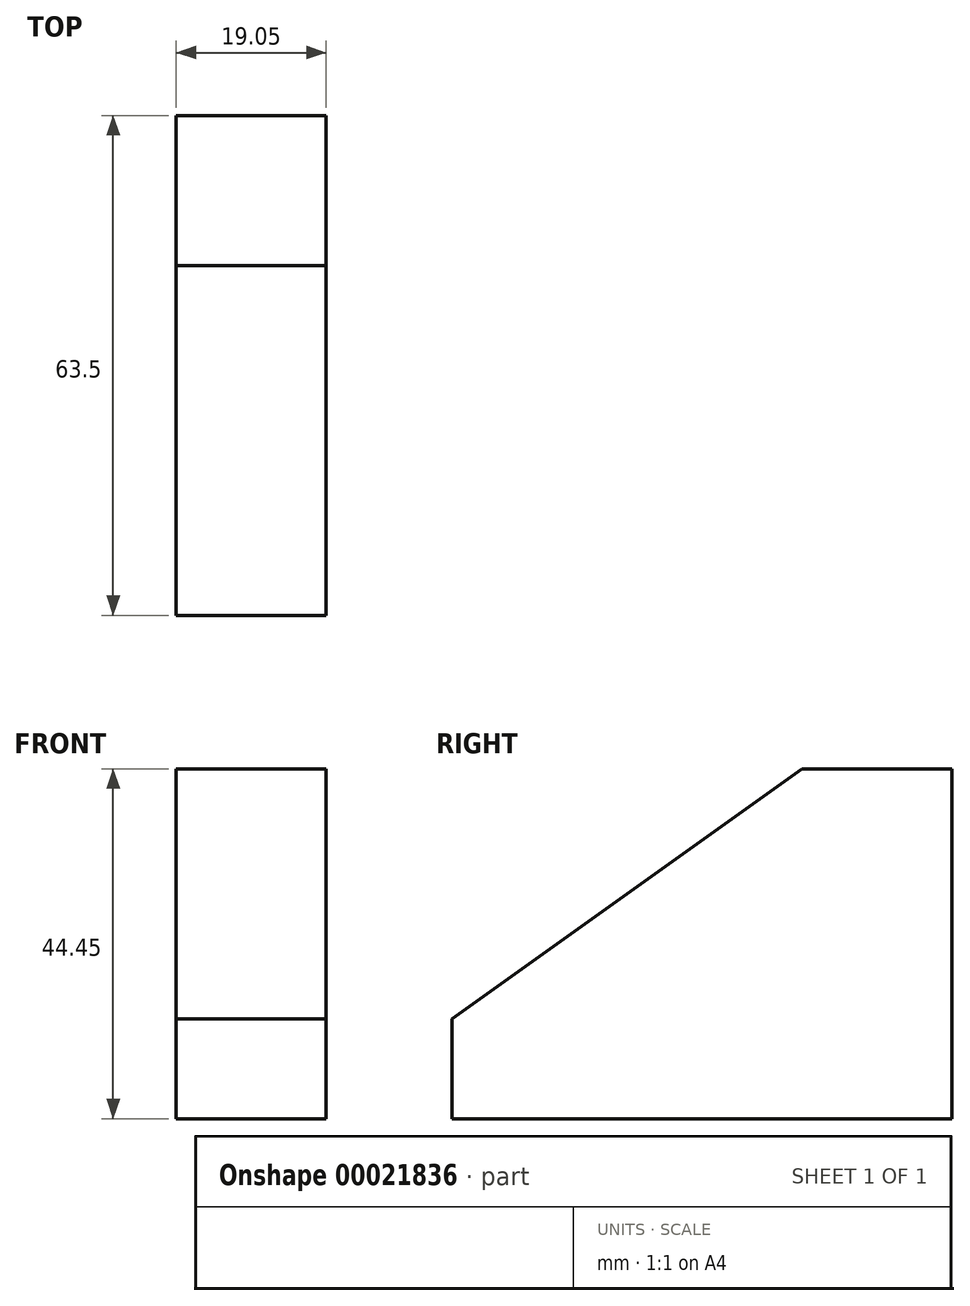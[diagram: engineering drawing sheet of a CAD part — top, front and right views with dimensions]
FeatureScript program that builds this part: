
annotation { "Feature Type Name" : "Feature", "Feature Type Description" : "" }
export const myFeature = defineFeature(function(context is Context, id is Id, definition is map)
    precondition{}
    {
        {
            var Q0;
            Q0=qCreatedBy(makeId("Right.planeOp"),FACE);
            var sketch = newSketch(context, id + "F0", { "sketchPlane" : qUnion([Q0])});
            skLineSegment(sketch, "E0.bottom", {"start": v(10.38, 27.08) * mm, "end": v(29.43, 27.08) * mm});
            skLineSegment(sketch, "E0.top", {"start": v(-34.07, -17.37) * mm, "end": v(29.43, -17.37) * mm});
            skLineSegment(sketch, "E0.left", {"start": v(-34.07, -4.67) * mm, "end": v(-34.07, -17.37) * mm});
            skLineSegment(sketch, "E0.right", {"start": v(29.43, 27.08) * mm, "end": v(29.43, -17.37) * mm});
            skLineSegment(sketch, "E1", {"start": v(-34.07, -4.67) * mm, "end": v(10.38, 27.08) * mm});
            skPoint(sketch, "E2.orphan", {"position": v(0, 27.08) * mm});
            skSolve(sketch);
        }
        {
            var Q0;
            Q0=makeQuery(id+"F0.imprint","IMPRINT",FACE,{"disambiguationData":[TD([[makeQuery(id+"F0.imprint","IMPRINT",EDGE,{"derivedFrom":sQuery(id+"F0.wireOp",EDGE,"E0.bottom")}),-1.0]])]});
            extrude(context, id + "F1", {"entities" : qUnion([Q0]), "depth" : 19.05 * mm});
        }
    });
